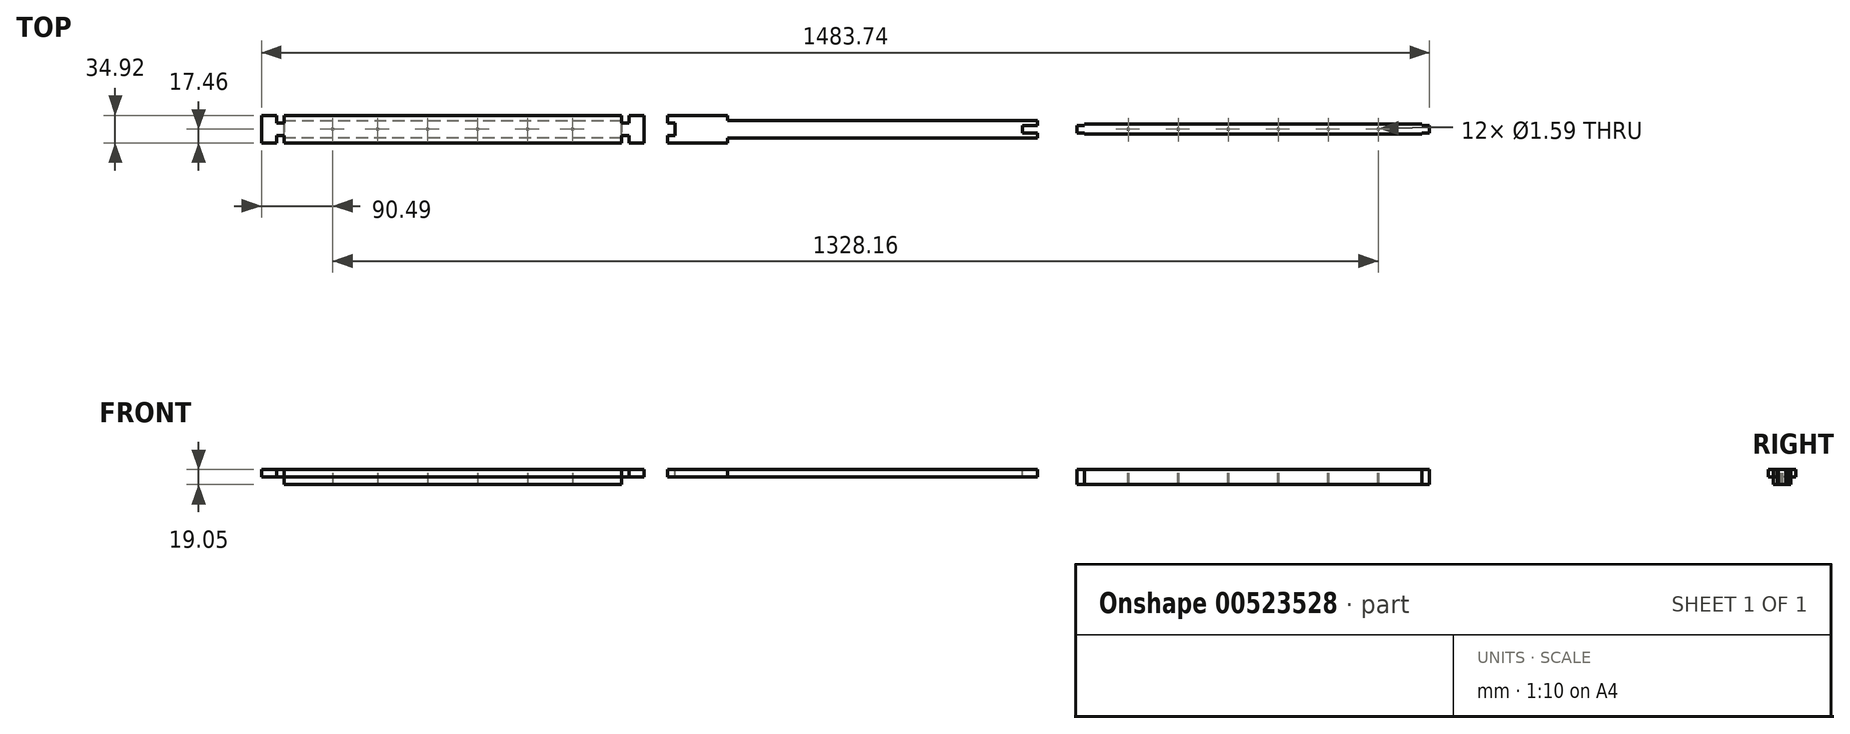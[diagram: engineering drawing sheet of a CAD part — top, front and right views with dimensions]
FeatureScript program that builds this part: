
annotation { "Feature Type Name" : "Feature", "Feature Type Description" : "" }
export const myFeature = defineFeature(function(context is Context, id is Id, definition is map)
    precondition{}
    {
        {
            var Q0;
            Q0=qCreatedBy(makeId("Top.planeOp"),FACE);
            var sketch = newSketch(context, id + "F0", { "sketchPlane" : qUnion([Q0])});
            skLineSegment(sketch, "E0", {"start": v(0, 0) * mm, "end": v(214.31, 0) * mm, "construction": true});
            skLineSegment(sketch, "E1", {"start": v(214.31, 0) * mm, "end": v(223.84, 0) * mm, "construction": true});
            skLineSegment(sketch, "E2", {"start": v(223.84, 0) * mm, "end": v(242.89, 0) * mm, "construction": true});
            skLineSegment(sketch, "E3", {"start": v(0, 0) * mm, "end": v(0, 7.94) * mm, "construction": true});
            skLineSegment(sketch, "E4", {"start": v(0, 7.94) * mm, "end": v(0, 11.11) * mm, "construction": true});
            skLineSegment(sketch, "E5", {"start": v(0, 11.11) * mm, "end": v(0, 17.46) * mm, "construction": true});
            skLineSegment(sketch, "E6", {"start": v(0, 0) * mm, "end": v(0, 17.46) * mm});
            skLineSegment(sketch, "E7", {"start": v(0, 17.46) * mm, "end": v(214.31, 17.46) * mm});
            skLineSegment(sketch, "E8", {"start": v(214.31, 17.46) * mm, "end": v(214.31, 7.94) * mm});
            skLineSegment(sketch, "E9", {"start": v(214.31, 7.94) * mm, "end": v(223.84, 7.94) * mm});
            skLineSegment(sketch, "E10", {"start": v(223.84, 7.94) * mm, "end": v(223.84, 17.46) * mm});
            skLineSegment(sketch, "E11", {"start": v(223.84, 17.46) * mm, "end": v(242.89, 17.46) * mm});
            skLineSegment(sketch, "E12", {"start": v(242.89, 17.46) * mm, "end": v(242.89, 0) * mm});
            skLineSegment(sketch, "E13", {"start": v(0, 11.11) * mm, "end": v(214.31, 11.11) * mm});
            skLineSegment(sketch, "E14", {"start": v(214.31, 7.94) * mm, "end": v(214.31, 0) * mm});
            skLineSegment(sketch, "E15.MirrorCS", {"start": v(0, -7.94) * mm, "end": v(0, -11.11) * mm, "construction": true});
            skLineSegment(sketch, "E16.MirrorCS", {"start": v(0, -11.11) * mm, "end": v(0, -17.46) * mm, "construction": true});
            skLineSegment(sketch, "E17.MirrorCS", {"start": v(0, 0) * mm, "end": v(0, -7.94) * mm, "construction": true});
            skLineSegment(sketch, "E18.MirrorCS", {"start": v(0, -11.11) * mm, "end": v(214.31, -11.11) * mm});
            skLineSegment(sketch, "E19.MirrorCS", {"start": v(0, 0) * mm, "end": v(0, -17.46) * mm});
            skLineSegment(sketch, "E20.MirrorCS", {"start": v(223.84, -17.46) * mm, "end": v(242.89, -17.46) * mm});
            skLineSegment(sketch, "E21.MirrorCS", {"start": v(242.89, -17.46) * mm, "end": v(242.89, 0) * mm});
            skLineSegment(sketch, "E22.MirrorCS", {"start": v(214.31, -17.46) * mm, "end": v(214.31, -7.94) * mm});
            skLineSegment(sketch, "E23.MirrorCS", {"start": v(214.31, -7.94) * mm, "end": v(223.84, -7.94) * mm});
            skLineSegment(sketch, "E24.MirrorCS", {"start": v(0, -17.46) * mm, "end": v(214.31, -17.46) * mm});
            skLineSegment(sketch, "E25.MirrorCS", {"start": v(214.31, -7.94) * mm, "end": v(214.31, 0) * mm});
            skLineSegment(sketch, "E26.MirrorCS", {"start": v(223.84, -7.94) * mm, "end": v(223.84, -17.46) * mm});
            skLineSegment(sketch, "E27.MirrorCS", {"start": v(0, 0) * mm, "end": v(-214.31, 0) * mm, "construction": true});
            skLineSegment(sketch, "E28.MirrorCS", {"start": v(-214.31, 7.94) * mm, "end": v(-223.84, 7.94) * mm});
            skLineSegment(sketch, "E29.MirrorCS", {"start": v(-223.84, 17.46) * mm, "end": v(-242.89, 17.46) * mm});
            skLineSegment(sketch, "E30.MirrorCS", {"start": v(-223.84, -17.46) * mm, "end": v(-242.89, -17.46) * mm});
            skLineSegment(sketch, "E31.MirrorCS", {"start": v(-223.84, -7.94) * mm, "end": v(-223.84, -17.46) * mm});
            skLineSegment(sketch, "E32.MirrorCS", {"start": v(-214.31, -7.94) * mm, "end": v(-223.84, -7.94) * mm});
            skLineSegment(sketch, "E33.MirrorCS", {"start": v(-214.31, -17.46) * mm, "end": v(-214.31, -7.94) * mm});
            skLineSegment(sketch, "E34.MirrorCS", {"start": v(-223.84, 0) * mm, "end": v(-242.89, 0) * mm, "construction": true});
            skLineSegment(sketch, "E35.MirrorCS", {"start": v(0, -17.46) * mm, "end": v(-214.31, -17.46) * mm});
            skLineSegment(sketch, "E36.MirrorCS", {"start": v(-214.31, -7.94) * mm, "end": v(-214.31, 0) * mm});
            skLineSegment(sketch, "E37.MirrorCS", {"start": v(-214.31, 0) * mm, "end": v(-223.84, 0) * mm, "construction": true});
            skLineSegment(sketch, "E38.MirrorCS", {"start": v(0, 17.46) * mm, "end": v(-214.31, 17.46) * mm});
            skLineSegment(sketch, "E39.MirrorCS", {"start": v(-242.89, -17.46) * mm, "end": v(-242.89, 0) * mm});
            skLineSegment(sketch, "E40.MirrorCS", {"start": v(0, 11.11) * mm, "end": v(-214.31, 11.11) * mm});
            skLineSegment(sketch, "E41.MirrorCS", {"start": v(-214.31, 17.46) * mm, "end": v(-214.31, 7.94) * mm});
            skLineSegment(sketch, "E42.MirrorCS", {"start": v(-214.31, 7.94) * mm, "end": v(-214.31, 0) * mm});
            skLineSegment(sketch, "E43.MirrorCS", {"start": v(0, -11.11) * mm, "end": v(-214.31, -11.11) * mm});
            skLineSegment(sketch, "E44.MirrorCS", {"start": v(-242.89, 17.46) * mm, "end": v(-242.89, 0) * mm});
            skLineSegment(sketch, "E45.MirrorCS", {"start": v(-223.84, 7.94) * mm, "end": v(-223.84, 17.46) * mm});
            skLineSegment(sketch, "E46", {"start": v(272.76, 17.46) * mm, "end": v(349, 17.46) * mm});
            skLineSegment(sketch, "E47", {"start": v(349, 17.46) * mm, "end": v(349, 11.11) * mm});
            skLineSegment(sketch, "E48", {"start": v(349, 11.11) * mm, "end": v(742.7, 11.11) * mm});
            skLineSegment(sketch, "E49", {"start": v(272.76, 17.46) * mm, "end": v(272.76, 7.94) * mm});
            skLineSegment(sketch, "E50", {"start": v(272.76, 7.94) * mm, "end": v(282.28, 7.94) * mm});
            skLineSegment(sketch, "E51", {"start": v(282.28, 7.94) * mm, "end": v(282.28, -7.94) * mm});
            skLineSegment(sketch, "E52", {"start": v(282.28, -7.94) * mm, "end": v(272.76, -7.94) * mm});
            skLineSegment(sketch, "E53", {"start": v(272.76, -7.94) * mm, "end": v(272.76, -17.46) * mm});
            skLineSegment(sketch, "E54", {"start": v(272.76, -17.46) * mm, "end": v(349, -17.46) * mm});
            skLineSegment(sketch, "E55", {"start": v(349, -17.46) * mm, "end": v(349, -11.11) * mm});
            skLineSegment(sketch, "E56", {"start": v(349, -11.11) * mm, "end": v(742.7, -11.11) * mm});
            skLineSegment(sketch, "E57", {"start": v(742.7, 11.11) * mm, "end": v(742.7, 4.76) * mm});
            skLineSegment(sketch, "E58", {"start": v(742.7, 4.76) * mm, "end": v(723.66, 4.76) * mm});
            skLineSegment(sketch, "E59", {"start": v(723.66, 4.76) * mm, "end": v(723.66, -4.76) * mm});
            skLineSegment(sketch, "E60", {"start": v(723.66, -4.76) * mm, "end": v(742.7, -4.76) * mm});
            skLineSegment(sketch, "E61", {"start": v(742.7, -4.76) * mm, "end": v(742.7, -11.11) * mm});
            skLineSegment(sketch, "E62", {"start": v(793.17, -4.76) * mm, "end": v(793.17, 4.76) * mm});
            skLineSegment(sketch, "E63", {"start": v(793.17, 4.76) * mm, "end": v(802.7, 4.76) * mm});
            skLineSegment(sketch, "E64", {"start": v(802.7, 4.76) * mm, "end": v(802.7, 6.35) * mm});
            skLineSegment(sketch, "E65", {"start": v(802.7, 6.35) * mm, "end": v(1231.32, 6.35) * mm});
            skLineSegment(sketch, "E66", {"start": v(1231.32, 6.35) * mm, "end": v(1231.32, 4.76) * mm});
            skLineSegment(sketch, "E67", {"start": v(1231.32, 4.76) * mm, "end": v(1240.85, 4.76) * mm});
            skLineSegment(sketch, "E68", {"start": v(1240.85, 4.76) * mm, "end": v(1240.85, -4.76) * mm});
            skLineSegment(sketch, "E69", {"start": v(1240.85, -4.76) * mm, "end": v(1231.32, -4.76) * mm});
            skLineSegment(sketch, "E70", {"start": v(1231.32, -4.76) * mm, "end": v(1231.32, -6.35) * mm});
            skLineSegment(sketch, "E71", {"start": v(1231.32, -6.35) * mm, "end": v(802.7, -6.35) * mm});
            skLineSegment(sketch, "E72", {"start": v(802.7, -6.35) * mm, "end": v(802.7, -4.76) * mm});
            skLineSegment(sketch, "E73", {"start": v(802.7, -4.76) * mm, "end": v(793.17, -4.76) * mm});
            skCircle(sketch, "E74", {"center": v(31.75, 0) * mm, "radius": 0.8 * mm});
            skCircle(sketch, "E75", {"center": v(95.25, 0) * mm, "radius": 0.8 * mm});
            skCircle(sketch, "E76", {"center": v(152.4, 0) * mm, "radius": 0.8 * mm});
            skCircle(sketch, "E77.MirrorC", {"center": v(-95.25, 0) * mm, "radius": 0.8 * mm});
            skCircle(sketch, "E78.MirrorC", {"center": v(-152.4, 0) * mm, "radius": 0.8 * mm});
            skCircle(sketch, "E79.MirrorC", {"center": v(-31.75, 0) * mm, "radius": 0.8 * mm});
            skLineSegment(sketch, "E80", {"start": v(793.17, 0) * mm, "end": v(1240.85, 0) * mm, "construction": true});
            skCircle(sketch, "E81", {"center": v(1175.76, 0) * mm, "radius": 0.8 * mm});
            skCircle(sketch, "E82", {"center": v(1112.26, 0) * mm, "radius": 0.8 * mm});
            skCircle(sketch, "E83", {"center": v(1048.76, 0) * mm, "radius": 0.8 * mm});
            skCircle(sketch, "E84", {"center": v(985.26, 0) * mm, "radius": 0.8 * mm});
            skCircle(sketch, "E85", {"center": v(858.26, 0) * mm, "radius": 0.8 * mm});
            skCircle(sketch, "E86", {"center": v(921.76, 0) * mm, "radius": 0.8 * mm});
            skSolve(sketch);
        }
        {
            var Q0;
            {var subQ1=sQuery(id+"F0.wireOp",EDGE,"E36.MirrorCS");Q0=makeQuery(id+"F0.imprint","IMPRINT",FACE,{"disambiguationData":[TD([[makeQuery(id+"F0.imprint","IMPRINT",EDGE,{"derivedFrom":subQ1}),-1.0]])]});}
            var Q1;
            {var subQ2=sQuery(id+"F0.wireOp",EDGE,"E13");Q1=makeQuery(id+"F0.imprint","IMPRINT",FACE,{"disambiguationData":[TD([[makeQuery(id+"F0.imprint","IMPRINT",EDGE,{"derivedFrom":subQ2}),-1.0]])]});}
            extrude(context, id + "F1", {"entities" : qUnion([Q0, Q1]), "oppositeDirection" : true, "depth" : 19.05 * mm, "offsetDistance" : 25.4 * mm});
        }
        {
            var Q0;
            Q0=makeQuery(id+"F0.imprint","IMPRINT",FACE,{"disambiguationData":[TD([[makeQuery(id+"F0.imprint","IMPRINT",EDGE,{"derivedFrom":sQuery(id+"F0.wireOp",EDGE,"E28.MirrorCS")}),1.0]])]});
            var Q1;
            Q1=makeQuery(id+"F0.imprint","IMPRINT",FACE,{"disambiguationData":[TD([[makeQuery(id+"F0.imprint","IMPRINT",EDGE,{"derivedFrom":sQuery(id+"F0.wireOp",EDGE,"E9")}),-1.0]])]});
            var Q2;
            {var subQ0=sQuery(id+"F0.wireOp",EDGE,"E7");Q2=makeQuery(id+"F0.imprint","IMPRINT",FACE,{"disambiguationData":[TD([[makeQuery(id+"F0.imprint","IMPRINT",EDGE,{"derivedFrom":subQ0}),-1.0]])]});}
            var Q3;
            {var subQ0=sQuery(id+"F0.wireOp",EDGE,"E38.MirrorCS");Q3=makeQuery(id+"F0.imprint","IMPRINT",FACE,{"disambiguationData":[TD([[makeQuery(id+"F0.imprint","IMPRINT",EDGE,{"derivedFrom":subQ0}),1.0]])]});}
            var Q4;
            {var subQ0=sQuery(id+"F0.wireOp",EDGE,"E35.MirrorCS");Q4=makeQuery(id+"F0.imprint","IMPRINT",FACE,{"disambiguationData":[TD([[makeQuery(id+"F0.imprint","IMPRINT",EDGE,{"derivedFrom":subQ0}),-1.0]])]});}
            var Q5;
            {var subQ0=sQuery(id+"F0.wireOp",EDGE,"E18.MirrorCS");Q5=makeQuery(id+"F0.imprint","IMPRINT",FACE,{"disambiguationData":[TD([[makeQuery(id+"F0.imprint","IMPRINT",EDGE,{"derivedFrom":subQ0}),-1.0]])]});}
            extrude(context, id + "F2", {"entities" : qUnion([Q0, Q1, Q2, Q3, Q4, Q5]), "operationType" : NewBodyOperationType.ADD, "oppositeDirection" : true, "depth" : 9.52 * mm, "offsetDistance" : 25.4 * mm});
        }
        {
            var Q0;
            Q0=makeQuery(id+"F0.imprint","IMPRINT",FACE,{"disambiguationData":[TD([[makeQuery(id+"F0.imprint","IMPRINT",EDGE,{"derivedFrom":sQuery(id+"F0.wireOp",EDGE,"E46")}),-1.0]])]});
            extrude(context, id + "F3", {"entities" : qUnion([Q0]), "oppositeDirection" : true, "depth" : 9.52 * mm, "offsetDistance" : 25.4 * mm});
        }
        {
            var Q0;
            Q0=makeQuery(id+"F0.imprint","IMPRINT",FACE,{"disambiguationData":[TD([[makeQuery(id+"F0.imprint","IMPRINT",EDGE,{"derivedFrom":sQuery(id+"F0.wireOp",EDGE,"E62")}),-1.0]])]});
            extrude(context, id + "F4", {"entities" : qUnion([Q0]), "oppositeDirection" : true, "depth" : 19.05 * mm, "offsetDistance" : 25.4 * mm});
        }
    });
